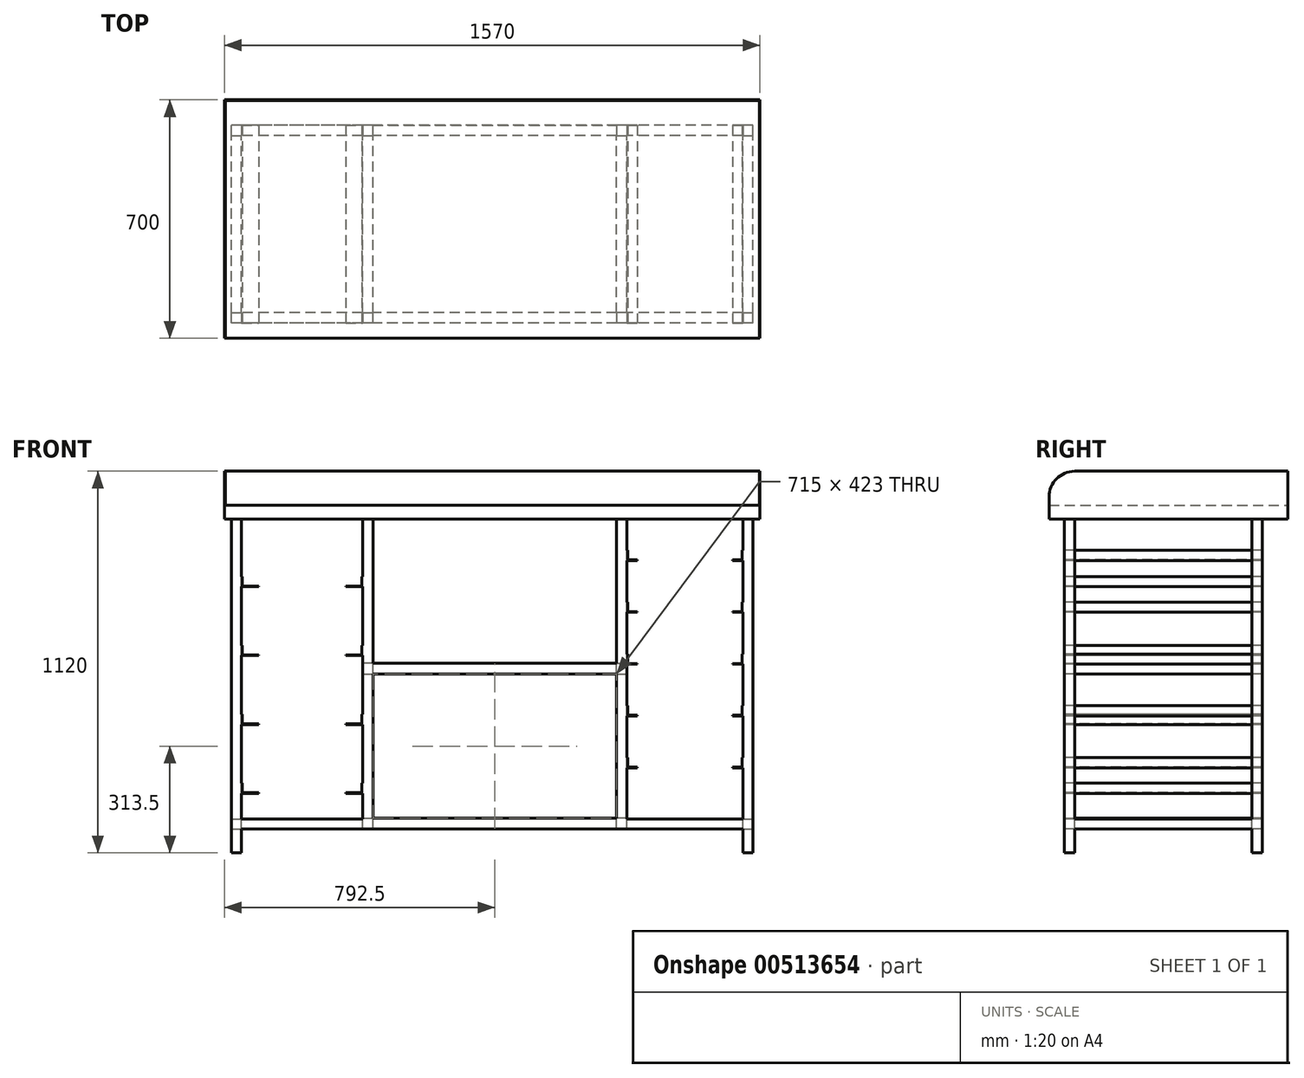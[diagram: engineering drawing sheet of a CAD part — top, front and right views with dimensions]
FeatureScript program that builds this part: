
annotation { "Feature Type Name" : "Feature", "Feature Type Description" : "" }
export const myFeature = defineFeature(function(context is Context, id is Id, definition is map)
    precondition{}
    {
        {
            var Q0;
            Q0=qCreatedBy(makeId("Top.planeOp"),FACE);
            var sketch = newSketch(context, id + "F0", { "sketchPlane" : qUnion([Q0])});
            skLineSegment(sketch, "E0.bottom", {"start": v(785, 350) * mm, "end": v(-785, 350) * mm});
            skLineSegment(sketch, "E0.top", {"start": v(785, -350) * mm, "end": v(-785, -350) * mm});
            skLineSegment(sketch, "E0.left", {"start": v(785, 350) * mm, "end": v(785, -350) * mm});
            skLineSegment(sketch, "E0.right", {"start": v(-785, 350) * mm, "end": v(-785, -350) * mm});
            skPoint(sketch, "E0.middle", {"position": v(0, 0) * mm});
            skSolve(sketch);
        }
        {
            var Q0;
            Q0 = qSketchRegion(id + "F0", true);
            extrude(context, id + "F1", {"entities" : qUnion([Q0]), "depth" : 40 * mm});
        }
        {
            var Q0;
            Q0=makeQuery(id+"F1.opExtrude","CAP_FACE",FACE,{"disambiguationData":[OSD([sQuery(id+"F0.wireOp",EDGE,"E0.bottom"),sQuery(id+"F0.wireOp",EDGE,"E0.top"),sQuery(id+"F0.wireOp",EDGE,"E0.left"),sQuery(id+"F0.wireOp",EDGE,"E0.right")])],"isStart":false});
            var sketch = newSketch(context, id + "F2", { "sketchPlane" : qUnion([Q0])});
            skLineSegment(sketch, "E1", {"start": v(-785, -350) * mm, "end": v(-785, 350) * mm});
            skLineSegment(sketch, "E2", {"start": v(-785, 350) * mm, "end": v(785, 350) * mm});
            skLineSegment(sketch, "E3", {"start": v(785, 350) * mm, "end": v(785, -350) * mm});
            skLineSegment(sketch, "E4", {"start": v(785, -350) * mm, "end": v(783, -350) * mm});
            skLineSegment(sketch, "E5", {"start": v(783, -350) * mm, "end": v(783, 348) * mm});
            skLineSegment(sketch, "E6", {"start": v(783, 348) * mm, "end": v(-783, 348) * mm});
            skLineSegment(sketch, "E7", {"start": v(-783, 348) * mm, "end": v(-783, -350) * mm});
            skLineSegment(sketch, "E8", {"start": v(-783, -350) * mm, "end": v(-785, -350) * mm});
            skSolve(sketch);
        }
        {
            var Q0;
            Q0 = qSketchRegion(id + "F2", true);
            extrude(context, id + "F3", {"entities" : qUnion([Q0]), "operationType" : NewBodyOperationType.ADD, "depth" : 100 * mm});
        }
        {
            var Q0;
            Q0=makeQuery(id+"F3.opExtrude","CAP_EDGE",EDGE,{"disambiguationData":[OSD([sQuery(id+"F2.wireOp",EDGE,"E8")])],"isStart":false});
            var Q1;
            Q1=makeQuery(id+"F3.opExtrude","CAP_EDGE",EDGE,{"disambiguationData":[OSD([sQuery(id+"F2.wireOp",EDGE,"E4")])],"isStart":false});
            fillet(context, id + "F4", {"entities" : qUnion([Q0, Q1]), "radius" : 75 * mm, "tangentPropagation" : true, "allowEdgeOverflow" : false});
        }
        {
            var Q0;
            Q0=makeQuery(id+"F1.opExtrude","CAP_FACE",FACE,{"disambiguationData":[OSD([sQuery(id+"F0.wireOp",EDGE,"E0.bottom"),sQuery(id+"F0.wireOp",EDGE,"E0.top"),sQuery(id+"F0.wireOp",EDGE,"E0.left"),sQuery(id+"F0.wireOp",EDGE,"E0.right")])],"isStart":true});
            var sketch = newSketch(context, id + "F5", { "sketchPlane" : qUnion([Q0])});
            skLineSegment(sketch, "E9.bottom", {"start": v(-735, 305) * mm, "end": v(-765, 305) * mm});
            skLineSegment(sketch, "E9.top", {"start": v(-735, 275) * mm, "end": v(-765, 275) * mm});
            skLineSegment(sketch, "E9.left", {"start": v(-735, 305) * mm, "end": v(-735, 275) * mm});
            skLineSegment(sketch, "E9.right", {"start": v(-765, 305) * mm, "end": v(-765, 275) * mm});
            skPoint(sketch, "E9.middle", {"position": v(-750, 290) * mm});
            skLineSegment(sketch, "E10.bottom", {"start": v(765, 305) * mm, "end": v(735, 305) * mm});
            skLineSegment(sketch, "E10.top", {"start": v(765, 275) * mm, "end": v(735, 275) * mm});
            skLineSegment(sketch, "E10.left", {"start": v(765, 305) * mm, "end": v(765, 275) * mm});
            skLineSegment(sketch, "E10.right", {"start": v(735, 305) * mm, "end": v(735, 275) * mm});
            skPoint(sketch, "E10.middle", {"position": v(750, 290) * mm});
            skPoint(sketch, "E10.middle.positionSnap0", {"position": v(-735, 290) * mm});
            skPoint(sketch, "E10.centerSnap0", {"position": v(-735, 290) * mm});
            skLineSegment(sketch, "E11.bottom", {"start": v(765, -245) * mm, "end": v(735, -245) * mm});
            skLineSegment(sketch, "E11.top", {"start": v(765, -275) * mm, "end": v(735, -275) * mm});
            skLineSegment(sketch, "E11.left", {"start": v(765, -245) * mm, "end": v(765, -275) * mm});
            skLineSegment(sketch, "E11.right", {"start": v(735, -245) * mm, "end": v(735, -275) * mm});
            skPoint(sketch, "E11.middle", {"position": v(750, -260) * mm});
            skLineSegment(sketch, "E12.bottom", {"start": v(-735, -245) * mm, "end": v(-765, -245) * mm});
            skLineSegment(sketch, "E12.top", {"start": v(-735, -275) * mm, "end": v(-765, -275) * mm});
            skLineSegment(sketch, "E12.left", {"start": v(-735, -245) * mm, "end": v(-735, -275) * mm});
            skLineSegment(sketch, "E12.right", {"start": v(-765, -245) * mm, "end": v(-765, -275) * mm});
            skPoint(sketch, "E12.middle", {"position": v(-750, -260) * mm});
            skPoint(sketch, "E12.middle.positionSnap0", {"position": v(735, -260) * mm});
            skPoint(sketch, "E12.centerSnap0", {"position": v(735, -260) * mm});
            skSolve(sketch);
        }
        {
            var Q0;
            Q0 = qSketchRegion(id + "F5", true);
            extrude(context, id + "F6", {"entities" : qUnion([Q0]), "operationType" : NewBodyOperationType.ADD, "depth" : (1050 - 40 - 30) * mm});
        }
        {
            var Q0;
            Q0=qCreatedBy(makeId("Right.planeOp"),FACE);
            var sketch = newSketch(context, id + "F7", { "sketchPlane" : qUnion([Q0])});
            skLineSegment(sketch, "E13.bottom", {"start": v(-275, -880) * mm, "end": v(-305, -880) * mm});
            skLineSegment(sketch, "E13.top", {"start": v(-275, -910) * mm, "end": v(-305, -910) * mm});
            skLineSegment(sketch, "E13.left", {"start": v(-275, -880) * mm, "end": v(-275, -910) * mm});
            skLineSegment(sketch, "E13.right", {"start": v(-305, -880) * mm, "end": v(-305, -910) * mm});
            skPoint(sketch, "E13.middle", {"position": v(-290, -895) * mm});
            skLineSegment(sketch, "E14.bottom", {"start": v(275, -880) * mm, "end": v(245, -880) * mm});
            skLineSegment(sketch, "E14.top", {"start": v(275, -910) * mm, "end": v(245, -910) * mm});
            skLineSegment(sketch, "E14.left", {"start": v(275, -880) * mm, "end": v(275, -910) * mm});
            skLineSegment(sketch, "E14.right", {"start": v(245, -880) * mm, "end": v(245, -910) * mm});
            skPoint(sketch, "E14.middle", {"position": v(260, -895) * mm});
            skSolve(sketch);
        }
        {
            var Q0;
            Q0 = qSketchRegion(id + "F7", true);
            extrude(context, id + "F8", {"entities" : qUnion([Q0]), "operationType" : NewBodyOperationType.ADD, "endBound" : BoundingType.UP_TO_NEXT, "depth" : 25 * mm, "hasSecondDirection" : true, "secondDirectionBound" : SecondDirectionBoundingType.UP_TO_NEXT, "secondDirectionOppositeDirection" : true, "secondDirectionDepth" : 25 * mm});
        }
        {
            var Q0;
            Q0=qCreatedBy(makeId("Front.planeOp"),FACE);
            var sketch = newSketch(context, id + "F9", { "sketchPlane" : qUnion([Q0])});
            skLineSegment(sketch, "E15.bottom", {"start": v(-735, -880) * mm, "end": v(-765, -880) * mm});
            skLineSegment(sketch, "E15.top", {"start": v(-735, -910) * mm, "end": v(-765, -910) * mm});
            skLineSegment(sketch, "E15.left", {"start": v(-735, -880) * mm, "end": v(-735, -910) * mm});
            skLineSegment(sketch, "E15.right", {"start": v(-765, -880) * mm, "end": v(-765, -910) * mm});
            skPoint(sketch, "E15.middle", {"position": v(-750, -895) * mm});
            skLineSegment(sketch, "E16.bottom", {"start": v(765, -880) * mm, "end": v(735, -880) * mm});
            skLineSegment(sketch, "E16.top", {"start": v(765, -910) * mm, "end": v(735, -910) * mm});
            skLineSegment(sketch, "E16.left", {"start": v(765, -880) * mm, "end": v(765, -910) * mm});
            skLineSegment(sketch, "E16.right", {"start": v(735, -880) * mm, "end": v(735, -910) * mm});
            skPoint(sketch, "E16.middle", {"position": v(750, -895) * mm});
            skSolve(sketch);
        }
        {
            var Q0;
            Q0 = qSketchRegion(id + "F9", true);
            extrude(context, id + "F10", {"entities" : qUnion([Q0]), "operationType" : NewBodyOperationType.ADD, "endBound" : BoundingType.UP_TO_NEXT, "depth" : 25 * mm, "hasSecondDirection" : true, "secondDirectionBound" : SecondDirectionBoundingType.UP_TO_NEXT, "secondDirectionOppositeDirection" : true, "secondDirectionDepth" : 25 * mm});
        }
        {
            var Q0;
            Q0=makeQuery(id+"F1.opExtrude","CAP_FACE",FACE,{"disambiguationData":[OSD([sQuery(id+"F0.wireOp",EDGE,"E0.bottom"),sQuery(id+"F0.wireOp",EDGE,"E0.top"),sQuery(id+"F0.wireOp",EDGE,"E0.left"),sQuery(id+"F0.wireOp",EDGE,"E0.right")])],"isStart":true});
            var sketch = newSketch(context, id + "F11", { "sketchPlane" : qUnion([Q0])});
            skLineSegment(sketch, "E17.bottom", {"start": v(-350, 305) * mm, "end": v(-380, 305) * mm});
            skLineSegment(sketch, "E17.top", {"start": v(-350, 275) * mm, "end": v(-380, 275) * mm});
            skLineSegment(sketch, "E17.left", {"start": v(-350, 305) * mm, "end": v(-350, 275) * mm});
            skLineSegment(sketch, "E17.right", {"start": v(-380, 305) * mm, "end": v(-380, 275) * mm});
            skPoint(sketch, "E17.middle", {"position": v(-365, 290) * mm});
            skLineSegment(sketch, "E18.bottom", {"start": v(395, 305) * mm, "end": v(365, 305) * mm});
            skLineSegment(sketch, "E18.top", {"start": v(395, 275) * mm, "end": v(365, 275) * mm});
            skLineSegment(sketch, "E18.left", {"start": v(395, 305) * mm, "end": v(395, 275) * mm});
            skLineSegment(sketch, "E18.right", {"start": v(365, 305) * mm, "end": v(365, 275) * mm});
            skPoint(sketch, "E18.middle", {"position": v(380, 290) * mm});
            skLineSegment(sketch, "E19.bottom", {"start": v(395, -245) * mm, "end": v(365, -245) * mm});
            skLineSegment(sketch, "E19.top", {"start": v(395, -275) * mm, "end": v(365, -275) * mm});
            skLineSegment(sketch, "E19.left", {"start": v(395, -245) * mm, "end": v(395, -275) * mm});
            skLineSegment(sketch, "E19.right", {"start": v(365, -245) * mm, "end": v(365, -275) * mm});
            skPoint(sketch, "E19.middle", {"position": v(380, -260) * mm});
            skPoint(sketch, "E19.middle.positionSnap0", {"position": v(380, 275) * mm});
            skPoint(sketch, "E19.centerSnap0", {"position": v(380, 275) * mm});
            skLineSegment(sketch, "E20.bottom", {"start": v(-350, -245) * mm, "end": v(-380, -245) * mm});
            skLineSegment(sketch, "E20.top", {"start": v(-350, -275) * mm, "end": v(-380, -275) * mm});
            skLineSegment(sketch, "E20.left", {"start": v(-350, -245) * mm, "end": v(-350, -275) * mm});
            skLineSegment(sketch, "E20.right", {"start": v(-380, -245) * mm, "end": v(-380, -275) * mm});
            skPoint(sketch, "E20.middle", {"position": v(-365, -260) * mm});
            skPoint(sketch, "E20.middle.positionSnap0", {"position": v(365, -260) * mm});
            skPoint(sketch, "E20.centerSnap0", {"position": v(365, -260) * mm});
            skSolve(sketch);
        }
        {
            var Q0;
            Q0 = qSketchRegion(id + "F11", true);
            extrude(context, id + "F12", {"entities" : qUnion([Q0]), "operationType" : NewBodyOperationType.ADD, "endBound" : BoundingType.UP_TO_NEXT, "depth" : 25 * mm});
        }
        {
            var Q0;
            Q0=qCreatedBy(makeId("Right.planeOp"),FACE);
            var sketch = newSketch(context, id + "F13", { "sketchPlane" : qUnion([Q0])});
            skLineSegment(sketch, "E21.bottom", {"start": v(-275, -425) * mm, "end": v(-305, -425) * mm});
            skLineSegment(sketch, "E21.top", {"start": v(-275, -455) * mm, "end": v(-305, -455) * mm});
            skLineSegment(sketch, "E21.left", {"start": v(-275, -425) * mm, "end": v(-275, -455) * mm});
            skLineSegment(sketch, "E21.right", {"start": v(-305, -425) * mm, "end": v(-305, -455) * mm});
            skPoint(sketch, "E21.middle", {"position": v(-290, -440) * mm});
            skLineSegment(sketch, "E22.bottom", {"start": v(275, -425) * mm, "end": v(245, -425) * mm});
            skLineSegment(sketch, "E22.top", {"start": v(275, -455) * mm, "end": v(245, -455) * mm});
            skLineSegment(sketch, "E22.left", {"start": v(275, -425) * mm, "end": v(275, -455) * mm});
            skLineSegment(sketch, "E22.right", {"start": v(245, -425) * mm, "end": v(245, -455) * mm});
            skPoint(sketch, "E22.middle", {"position": v(260, -440) * mm});
            skSolve(sketch);
        }
        {
            var Q0;
            Q0 = qSketchRegion(id + "F13", true);
            extrude(context, id + "F14", {"entities" : qUnion([Q0]), "operationType" : NewBodyOperationType.ADD, "endBound" : BoundingType.UP_TO_NEXT, "depth" : 25 * mm, "hasSecondDirection" : true, "secondDirectionBound" : SecondDirectionBoundingType.UP_TO_NEXT, "secondDirectionOppositeDirection" : true, "secondDirectionDepth" : 25 * mm});
        }
        {
            var Q0;
            Q0=qCreatedBy(makeId("Front.planeOp"),FACE);
            var sketch = newSketch(context, id + "F15", { "sketchPlane" : qUnion([Q0])});
            skLineSegment(sketch, "E23.bottom", {"start": v(-350, -425) * mm, "end": v(-380, -425) * mm});
            skLineSegment(sketch, "E23.top", {"start": v(-350, -455) * mm, "end": v(-380, -455) * mm});
            skLineSegment(sketch, "E23.left", {"start": v(-350, -425) * mm, "end": v(-350, -455) * mm});
            skLineSegment(sketch, "E23.right", {"start": v(-380, -425) * mm, "end": v(-380, -455) * mm});
            skPoint(sketch, "E23.middle", {"position": v(-365, -440) * mm});
            skLineSegment(sketch, "E24.bottom", {"start": v(395, -425) * mm, "end": v(365, -425) * mm});
            skLineSegment(sketch, "E24.top", {"start": v(395, -455) * mm, "end": v(365, -455) * mm});
            skLineSegment(sketch, "E24.left", {"start": v(395, -425) * mm, "end": v(395, -455) * mm});
            skLineSegment(sketch, "E24.right", {"start": v(365, -425) * mm, "end": v(365, -455) * mm});
            skPoint(sketch, "E24.middle", {"position": v(380, -440) * mm});
            skLineSegment(sketch, "E25.bottom", {"start": v(395, -880) * mm, "end": v(365, -880) * mm});
            skLineSegment(sketch, "E25.top", {"start": v(395, -910) * mm, "end": v(365, -910) * mm});
            skLineSegment(sketch, "E25.left", {"start": v(395, -880) * mm, "end": v(395, -910) * mm});
            skLineSegment(sketch, "E25.right", {"start": v(365, -880) * mm, "end": v(365, -910) * mm});
            skPoint(sketch, "E25.middle", {"position": v(380, -895) * mm});
            skPoint(sketch, "E25.middle.positionSnap0", {"position": v(380, -455) * mm});
            skPoint(sketch, "E25.centerSnap0", {"position": v(380, -455) * mm});
            skLineSegment(sketch, "E26.bottom", {"start": v(-350, -880) * mm, "end": v(-380, -880) * mm});
            skLineSegment(sketch, "E26.top", {"start": v(-350, -910) * mm, "end": v(-380, -910) * mm});
            skLineSegment(sketch, "E26.left", {"start": v(-350, -880) * mm, "end": v(-350, -910) * mm});
            skLineSegment(sketch, "E26.right", {"start": v(-380, -880) * mm, "end": v(-380, -910) * mm});
            skPoint(sketch, "E26.middle", {"position": v(-365, -895) * mm});
            skSolve(sketch);
        }
        {
            var Q0;
            Q0 = qSketchRegion(id + "F15", true);
            extrude(context, id + "F16", {"entities" : qUnion([Q0]), "operationType" : NewBodyOperationType.ADD, "endBound" : BoundingType.UP_TO_NEXT, "depth" : 25 * mm, "hasSecondDirection" : true, "secondDirectionBound" : SecondDirectionBoundingType.UP_TO_NEXT, "secondDirectionOppositeDirection" : true, "secondDirectionDepth" : 25 * mm});
        }
        {
            var Q0;
            Q0=makeQuery(id+"F14.opExtrude","SWEPT_FACE",FACE,{"disambiguationData":[OSD([sQuery(id+"F13.wireOp",EDGE,"E22.bottom")])]});
            var sketch = newSketch(context, id + "F17", { "sketchPlane" : qUnion([Q0])});
            skLineSegment(sketch, "E27", {"start": v(365, 275) * mm, "end": v(365, 245) * mm});
            skLineSegment(sketch, "E28", {"start": v(365, 245) * mm, "end": v(395, 245) * mm});
            skLineSegment(sketch, "E29", {"start": v(395, 245) * mm, "end": v(395, -275) * mm});
            skLineSegment(sketch, "E30", {"start": v(395, -275) * mm, "end": v(365, -275) * mm});
            skLineSegment(sketch, "E31", {"start": v(365, -275) * mm, "end": v(365, -305) * mm});
            skLineSegment(sketch, "E32", {"start": v(365, -305) * mm, "end": v(-350, -305) * mm});
            skLineSegment(sketch, "E33", {"start": v(-350, -305) * mm, "end": v(-350, -275) * mm});
            skLineSegment(sketch, "E34", {"start": v(-350, -275) * mm, "end": v(-380, -275) * mm});
            skLineSegment(sketch, "E35", {"start": v(-380, -275) * mm, "end": v(-380, 245) * mm});
            skLineSegment(sketch, "E36", {"start": v(-380, 245) * mm, "end": v(-350, 245) * mm});
            skLineSegment(sketch, "E37", {"start": v(-350, 245) * mm, "end": v(-350, 275) * mm});
            skLineSegment(sketch, "E38", {"start": v(-350, 275) * mm, "end": v(365, 275) * mm});
            skSolve(sketch);
        }
        {
            var Q0;
            Q0 = qSketchRegion(id + "F17", true);
            extrude(context, id + "F18", {"entities" : qUnion([Q0]), "operationType" : NewBodyOperationType.ADD, "depth" : 2 * mm});
        }
        {
            var Q0;
            Q0=makeQuery(id+"F16.opExtrude","SWEPT_FACE",FACE,{"disambiguationData":[OSD([sQuery(id+"F15.wireOp",EDGE,"E26.bottom")])]});
            var sketch = newSketch(context, id + "F19", { "sketchPlane" : qUnion([Q0])});
            skLineSegment(sketch, "E39", {"start": v(365, 275) * mm, "end": v(365, 245) * mm});
            skLineSegment(sketch, "E40", {"start": v(365, 245) * mm, "end": v(395, 245) * mm});
            skLineSegment(sketch, "E41", {"start": v(395, 245) * mm, "end": v(395, -275) * mm});
            skLineSegment(sketch, "E42", {"start": v(395, -275) * mm, "end": v(365, -275) * mm});
            skLineSegment(sketch, "E43", {"start": v(365, -275) * mm, "end": v(365, -305) * mm});
            skLineSegment(sketch, "E44", {"start": v(365, -305) * mm, "end": v(-350, -305) * mm});
            skLineSegment(sketch, "E45", {"start": v(-350, -305) * mm, "end": v(-350, -275) * mm});
            skLineSegment(sketch, "E46", {"start": v(-350, -275) * mm, "end": v(-380, -275) * mm});
            skLineSegment(sketch, "E47", {"start": v(-380, -275) * mm, "end": v(-380, 245) * mm});
            skLineSegment(sketch, "E48", {"start": v(-380, 245) * mm, "end": v(-350, 245) * mm});
            skLineSegment(sketch, "E49", {"start": v(-350, 245) * mm, "end": v(-350, 275) * mm});
            skLineSegment(sketch, "E50", {"start": v(-350, 275) * mm, "end": v(365, 275) * mm});
            skSolve(sketch);
        }
        {
            var Q0;
            Q0 = qSketchRegion(id + "F19", true);
            extrude(context, id + "F20", {"entities" : qUnion([Q0]), "operationType" : NewBodyOperationType.ADD, "depth" : 2 * mm});
        }
        {
            var Q0;
            Q0=makeQuery(id+"F20.boolean.opBoolean","MERGE",FACE,{"derivedFrom":[makeQuery(id+"F18.boolean.opBoolean","MERGE",FACE,{"derivedFrom":[makeQuery(id+"F14.boolean.opBoolean","MERGE",FACE,{"derivedFrom":[makeQuery(id+"F12.boolean.opBoolean","MERGE",FACE,{"derivedFrom":[makeQuery(id+"F8.boolean.opBoolean","MERGE",FACE,{"derivedFrom":[makeQuery(id+"F6.opExtrude","SWEPT_FACE",FACE,{"disambiguationData":[OSD([sQuery(id+"F5.wireOp",EDGE,"E9.bottom")])]}),makeQuery(id+"F6.opExtrude","SWEPT_FACE",FACE,{"disambiguationData":[OSD([sQuery(id+"F5.wireOp",EDGE,"E10.bottom")])]}),makeQuery(id+"F8.opExtrude","SWEPT_FACE",FACE,{"disambiguationData":[OSD([sQuery(id+"F7.wireOp",EDGE,"E13.right")])]})]}),makeQuery(id+"F12.opExtrude","SWEPT_FACE",FACE,{"disambiguationData":[OSD([sQuery(id+"F11.wireOp",EDGE,"E17.bottom")])]}),makeQuery(id+"F12.opExtrude","SWEPT_FACE",FACE,{"disambiguationData":[OSD([sQuery(id+"F11.wireOp",EDGE,"E18.bottom")])]})]}),makeQuery(id+"F14.opExtrude","SWEPT_FACE",FACE,{"disambiguationData":[OSD([sQuery(id+"F13.wireOp",EDGE,"E21.right")])]})]}),makeQuery(id+"F18.opExtrude","SWEPT_FACE",FACE,{"disambiguationData":[OSD([sQuery(id+"F17.wireOp",EDGE,"E32")])]})]}),makeQuery(id+"F20.opExtrude","SWEPT_FACE",FACE,{"disambiguationData":[OSD([sQuery(id+"F19.wireOp",EDGE,"E44")])]})]});
            var sketch = newSketch(context, id + "F21", { "sketchPlane" : qUnion([Q0])});
            skLineSegment(sketch, "E51", {"start": v(-735, -775) * mm, "end": v(-735, -805) * mm});
            skLineSegment(sketch, "E52", {"start": v(-735, -805) * mm, "end": v(-685, -805) * mm});
            skLineSegment(sketch, "E53", {"start": v(-685, -805) * mm, "end": v(-685, -803) * mm});
            skLineSegment(sketch, "E54", {"start": v(-685, -803) * mm, "end": v(-733, -803) * mm});
            skLineSegment(sketch, "E55", {"start": v(-733, -803) * mm, "end": v(-733, -775) * mm});
            skLineSegment(sketch, "E56", {"start": v(-733, -775) * mm, "end": v(-735, -775) * mm});
            skLineSegment(sketch, "E57.0.1.0", {"start": v(-735, -603) * mm, "end": v(-685, -603) * mm});
            skLineSegment(sketch, "E57.0.1.1", {"start": v(-685, -601) * mm, "end": v(-733, -601) * mm});
            skLineSegment(sketch, "E57.0.1.2", {"start": v(-733, -601) * mm, "end": v(-733, -573) * mm});
            skLineSegment(sketch, "E57.0.1.3", {"start": v(-735, -573) * mm, "end": v(-735, -603) * mm});
            skLineSegment(sketch, "E57.0.1.4", {"start": v(-685, -603) * mm, "end": v(-685, -601) * mm});
            skLineSegment(sketch, "E57.0.1.5", {"start": v(-733, -573) * mm, "end": v(-735, -573) * mm});
            skLineSegment(sketch, "E57.0.2.0", {"start": v(-735, -401) * mm, "end": v(-685, -401) * mm});
            skLineSegment(sketch, "E57.0.2.1", {"start": v(-685, -399) * mm, "end": v(-733, -399) * mm});
            skLineSegment(sketch, "E57.0.2.2", {"start": v(-733, -399) * mm, "end": v(-733, -371) * mm});
            skLineSegment(sketch, "E57.0.2.3", {"start": v(-735, -371) * mm, "end": v(-735, -401) * mm});
            skLineSegment(sketch, "E57.0.2.4", {"start": v(-685, -401) * mm, "end": v(-685, -399) * mm});
            skLineSegment(sketch, "E57.0.2.5", {"start": v(-733, -371) * mm, "end": v(-735, -371) * mm});
            skLineSegment(sketch, "E57.0.3.0", {"start": v(-735, -199) * mm, "end": v(-685, -199) * mm});
            skLineSegment(sketch, "E57.0.3.1", {"start": v(-685, -197) * mm, "end": v(-733, -197) * mm});
            skLineSegment(sketch, "E57.0.3.2", {"start": v(-733, -197) * mm, "end": v(-733, -169) * mm});
            skLineSegment(sketch, "E57.0.3.3", {"start": v(-735, -169) * mm, "end": v(-735, -199) * mm});
            skLineSegment(sketch, "E57.0.3.4", {"start": v(-685, -199) * mm, "end": v(-685, -197) * mm});
            skLineSegment(sketch, "E57.0.3.5", {"start": v(-733, -169) * mm, "end": v(-735, -169) * mm});
            skLineSegment(sketch, "E57.direction1", {"start": v(-735, -805) * mm, "end": v(-710, -805) * mm, "construction": true});
            skLineSegment(sketch, "E57.direction2", {"start": v(-735, -805) * mm, "end": v(-735, -603) * mm, "construction": true});
            skLineSegment(sketch, "E58", {"start": v(-557.5, -880) * mm, "end": v(-557.5, -90.41) * mm, "construction": true});
            skLineSegment(sketch, "E59.MirrorCS", {"start": v(-430, -805) * mm, "end": v(-430, -803) * mm});
            skLineSegment(sketch, "E60.MirrorCS", {"start": v(-380, -775) * mm, "end": v(-380, -805) * mm});
            skLineSegment(sketch, "E61.MirrorCS", {"start": v(-380, -805) * mm, "end": v(-430, -805) * mm});
            skLineSegment(sketch, "E62.MirrorCS", {"start": v(-380, -805) * mm, "end": v(-405, -805) * mm, "construction": true});
            skLineSegment(sketch, "E63.MirrorCS", {"start": v(-430, -603) * mm, "end": v(-430, -601) * mm});
            skLineSegment(sketch, "E64.MirrorCS", {"start": v(-382, -601) * mm, "end": v(-382, -573) * mm});
            skLineSegment(sketch, "E65.MirrorCS", {"start": v(-382, -803) * mm, "end": v(-382, -775) * mm});
            skLineSegment(sketch, "E66.MirrorCS", {"start": v(-430, -401) * mm, "end": v(-430, -399) * mm});
            skLineSegment(sketch, "E67.MirrorCS", {"start": v(-430, -803) * mm, "end": v(-382, -803) * mm});
            skLineSegment(sketch, "E68.MirrorCS", {"start": v(-380, -573) * mm, "end": v(-380, -603) * mm});
            skLineSegment(sketch, "E69.MirrorCS", {"start": v(-382, -775) * mm, "end": v(-380, -775) * mm});
            skLineSegment(sketch, "E70.MirrorCS", {"start": v(-382, -573) * mm, "end": v(-380, -573) * mm});
            skLineSegment(sketch, "E71.MirrorCS", {"start": v(-382, -371) * mm, "end": v(-380, -371) * mm});
            skLineSegment(sketch, "E72.MirrorCS", {"start": v(-382, -399) * mm, "end": v(-382, -371) * mm});
            skLineSegment(sketch, "E73.MirrorCS", {"start": v(-380, -603) * mm, "end": v(-430, -603) * mm});
            skLineSegment(sketch, "E74.MirrorCS", {"start": v(-430, -399) * mm, "end": v(-382, -399) * mm});
            skLineSegment(sketch, "E75.MirrorCS", {"start": v(-380, -401) * mm, "end": v(-430, -401) * mm});
            skLineSegment(sketch, "E76.MirrorCS", {"start": v(-382, -169) * mm, "end": v(-380, -169) * mm});
            skLineSegment(sketch, "E77.MirrorCS", {"start": v(-380, -371) * mm, "end": v(-380, -401) * mm});
            skLineSegment(sketch, "E78.MirrorCS", {"start": v(-430, -601) * mm, "end": v(-382, -601) * mm});
            skLineSegment(sketch, "E79.MirrorCS", {"start": v(-430, -197) * mm, "end": v(-382, -197) * mm});
            skLineSegment(sketch, "E80.MirrorCS", {"start": v(-382, -197) * mm, "end": v(-382, -169) * mm});
            skLineSegment(sketch, "E81.MirrorCS", {"start": v(-380, -199) * mm, "end": v(-430, -199) * mm});
            skLineSegment(sketch, "E82.MirrorCS", {"start": v(-430, -199) * mm, "end": v(-430, -197) * mm});
            skLineSegment(sketch, "E83.MirrorCS", {"start": v(-380, -169) * mm, "end": v(-380, -199) * mm});
            skLineSegment(sketch, "E84.MirrorCS", {"start": v(-380, -805) * mm, "end": v(-380, -603) * mm, "construction": true});
            skSolve(sketch);
        }
        {
            var Q0;
            Q0 = qSketchRegion(id + "F21", true);
            var Q1;
            Q1=makeQuery(id+"F20.boolean.opBoolean","MERGE",FACE,{"derivedFrom":[makeQuery(id+"F18.boolean.opBoolean","MERGE",FACE,{"derivedFrom":[makeQuery(id+"F14.boolean.opBoolean","MERGE",FACE,{"derivedFrom":[makeQuery(id+"F12.boolean.opBoolean","MERGE",FACE,{"derivedFrom":[makeQuery(id+"F8.boolean.opBoolean","MERGE",FACE,{"derivedFrom":[makeQuery(id+"F6.opExtrude","SWEPT_FACE",FACE,{"disambiguationData":[OSD([sQuery(id+"F5.wireOp",EDGE,"E11.top")])]}),makeQuery(id+"F6.opExtrude","SWEPT_FACE",FACE,{"disambiguationData":[OSD([sQuery(id+"F5.wireOp",EDGE,"E12.top")])]}),makeQuery(id+"F8.opExtrude","SWEPT_FACE",FACE,{"disambiguationData":[OSD([sQuery(id+"F7.wireOp",EDGE,"E14.left")])]})]}),makeQuery(id+"F12.opExtrude","SWEPT_FACE",FACE,{"disambiguationData":[OSD([sQuery(id+"F11.wireOp",EDGE,"E19.top")])]}),makeQuery(id+"F12.opExtrude","SWEPT_FACE",FACE,{"disambiguationData":[OSD([sQuery(id+"F11.wireOp",EDGE,"E20.top")])]})]}),makeQuery(id+"F14.opExtrude","SWEPT_FACE",FACE,{"disambiguationData":[OSD([sQuery(id+"F13.wireOp",EDGE,"E22.left")])]})]}),makeQuery(id+"F18.opExtrude","SWEPT_FACE",FACE,{"disambiguationData":[OSD([sQuery(id+"F17.wireOp",EDGE,"E38")])]})]}),makeQuery(id+"F20.opExtrude","SWEPT_FACE",FACE,{"disambiguationData":[OSD([sQuery(id+"F19.wireOp",EDGE,"E50")])]})]});
            extrude(context, id + "F22", {"entities" : qUnion([Q0]), "operationType" : NewBodyOperationType.ADD, "endBound" : BoundingType.UP_TO_SURFACE, "oppositeDirection" : true, "endBoundEntityFace" : qUnion([Q1]), "depth" : 25 * mm});
        }
        {
            var Q0;
            Q0=makeQuery(id+"F22.boolean.opBoolean","MERGE",FACE,{"derivedFrom":[makeQuery(id+"F20.boolean.opBoolean","MERGE",FACE,{"derivedFrom":[makeQuery(id+"F18.boolean.opBoolean","MERGE",FACE,{"derivedFrom":[makeQuery(id+"F14.boolean.opBoolean","MERGE",FACE,{"derivedFrom":[makeQuery(id+"F12.boolean.opBoolean","MERGE",FACE,{"derivedFrom":[makeQuery(id+"F8.boolean.opBoolean","MERGE",FACE,{"derivedFrom":[makeQuery(id+"F6.opExtrude","SWEPT_FACE",FACE,{"disambiguationData":[OSD([sQuery(id+"F5.wireOp",EDGE,"E9.bottom")])]}),makeQuery(id+"F6.opExtrude","SWEPT_FACE",FACE,{"disambiguationData":[OSD([sQuery(id+"F5.wireOp",EDGE,"E10.bottom")])]}),makeQuery(id+"F8.opExtrude","SWEPT_FACE",FACE,{"disambiguationData":[OSD([sQuery(id+"F7.wireOp",EDGE,"E13.right")])]})]}),makeQuery(id+"F12.opExtrude","SWEPT_FACE",FACE,{"disambiguationData":[OSD([sQuery(id+"F11.wireOp",EDGE,"E17.bottom")])]}),makeQuery(id+"F12.opExtrude","SWEPT_FACE",FACE,{"disambiguationData":[OSD([sQuery(id+"F11.wireOp",EDGE,"E18.bottom")])]})]}),makeQuery(id+"F14.opExtrude","SWEPT_FACE",FACE,{"disambiguationData":[OSD([sQuery(id+"F13.wireOp",EDGE,"E21.right")])]})]}),makeQuery(id+"F18.opExtrude","SWEPT_FACE",FACE,{"disambiguationData":[OSD([sQuery(id+"F17.wireOp",EDGE,"E32")])]})]}),makeQuery(id+"F20.opExtrude","SWEPT_FACE",FACE,{"disambiguationData":[OSD([sQuery(id+"F19.wireOp",EDGE,"E44")])]})]}),makeQuery(id+"F22.opExtrude","CAP_FACE",FACE,{"disambiguationData":[OSD([sQuery(id+"F21.wireOp",EDGE,"E51"),sQuery(id+"F21.wireOp",EDGE,"E52"),sQuery(id+"F21.wireOp",EDGE,"E53"),sQuery(id+"F21.wireOp",EDGE,"E54"),sQuery(id+"F21.wireOp",EDGE,"E55"),sQuery(id+"F21.wireOp",EDGE,"E56")])],"isStart":true}),makeQuery(id+"F22.opExtrude","CAP_FACE",FACE,{"disambiguationData":[OSD([sQuery(id+"F21.wireOp",EDGE,"E57.0.1.0"),sQuery(id+"F21.wireOp",EDGE,"E57.0.1.1"),sQuery(id+"F21.wireOp",EDGE,"E57.0.1.2"),sQuery(id+"F21.wireOp",EDGE,"E57.0.1.3"),sQuery(id+"F21.wireOp",EDGE,"E57.0.1.4"),sQuery(id+"F21.wireOp",EDGE,"E57.0.1.5")])],"isStart":true}),makeQuery(id+"F22.opExtrude","CAP_FACE",FACE,{"disambiguationData":[OSD([sQuery(id+"F21.wireOp",EDGE,"E57.0.2.0"),sQuery(id+"F21.wireOp",EDGE,"E57.0.2.1"),sQuery(id+"F21.wireOp",EDGE,"E57.0.2.2"),sQuery(id+"F21.wireOp",EDGE,"E57.0.2.3"),sQuery(id+"F21.wireOp",EDGE,"E57.0.2.4"),sQuery(id+"F21.wireOp",EDGE,"E57.0.2.5")])],"isStart":true}),makeQuery(id+"F22.opExtrude","CAP_FACE",FACE,{"disambiguationData":[OSD([sQuery(id+"F21.wireOp",EDGE,"E57.0.3.0"),sQuery(id+"F21.wireOp",EDGE,"E57.0.3.1"),sQuery(id+"F21.wireOp",EDGE,"E57.0.3.2"),sQuery(id+"F21.wireOp",EDGE,"E57.0.3.3"),sQuery(id+"F21.wireOp",EDGE,"E57.0.3.4"),sQuery(id+"F21.wireOp",EDGE,"E57.0.3.5")])],"isStart":true}),makeQuery(id+"F22.opExtrude","CAP_FACE",FACE,{"disambiguationData":[OSD([sQuery(id+"F21.wireOp",EDGE,"E59.MirrorCS"),sQuery(id+"F21.wireOp",EDGE,"E60.MirrorCS"),sQuery(id+"F21.wireOp",EDGE,"E61.MirrorCS"),sQuery(id+"F21.wireOp",EDGE,"E65.MirrorCS"),sQuery(id+"F21.wireOp",EDGE,"E67.MirrorCS"),sQuery(id+"F21.wireOp",EDGE,"E69.MirrorCS")])],"isStart":true}),makeQuery(id+"F22.opExtrude","CAP_FACE",FACE,{"disambiguationData":[OSD([sQuery(id+"F21.wireOp",EDGE,"E63.MirrorCS"),sQuery(id+"F21.wireOp",EDGE,"E64.MirrorCS"),sQuery(id+"F21.wireOp",EDGE,"E68.MirrorCS"),sQuery(id+"F21.wireOp",EDGE,"E70.MirrorCS"),sQuery(id+"F21.wireOp",EDGE,"E73.MirrorCS"),sQuery(id+"F21.wireOp",EDGE,"E78.MirrorCS")])],"isStart":true}),makeQuery(id+"F22.opExtrude","CAP_FACE",FACE,{"disambiguationData":[OSD([sQuery(id+"F21.wireOp",EDGE,"E66.MirrorCS"),sQuery(id+"F21.wireOp",EDGE,"E71.MirrorCS"),sQuery(id+"F21.wireOp",EDGE,"E72.MirrorCS"),sQuery(id+"F21.wireOp",EDGE,"E74.MirrorCS"),sQuery(id+"F21.wireOp",EDGE,"E75.MirrorCS"),sQuery(id+"F21.wireOp",EDGE,"E77.MirrorCS")])],"isStart":true}),makeQuery(id+"F22.opExtrude","CAP_FACE",FACE,{"disambiguationData":[OSD([sQuery(id+"F21.wireOp",EDGE,"E76.MirrorCS"),sQuery(id+"F21.wireOp",EDGE,"E79.MirrorCS"),sQuery(id+"F21.wireOp",EDGE,"E80.MirrorCS"),sQuery(id+"F21.wireOp",EDGE,"E81.MirrorCS"),sQuery(id+"F21.wireOp",EDGE,"E82.MirrorCS"),sQuery(id+"F21.wireOp",EDGE,"E83.MirrorCS")])],"isStart":true})]});
            var sketch = newSketch(context, id + "F23", { "sketchPlane" : qUnion([Q0])});
            skLineSegment(sketch, "E85", {"start": v(395, -700) * mm, "end": v(395, -730) * mm});
            skLineSegment(sketch, "E86", {"start": v(395, -730) * mm, "end": v(425, -730) * mm});
            skLineSegment(sketch, "E87", {"start": v(425, -730) * mm, "end": v(425, -728) * mm});
            skLineSegment(sketch, "E88", {"start": v(425, -728) * mm, "end": v(397, -728) * mm});
            skLineSegment(sketch, "E89", {"start": v(397, -728) * mm, "end": v(397, -700) * mm});
            skLineSegment(sketch, "E90", {"start": v(397, -700) * mm, "end": v(395, -700) * mm});
            skLineSegment(sketch, "E91.0.1.0", {"start": v(395, -548) * mm, "end": v(395, -578) * mm});
            skLineSegment(sketch, "E91.0.1.1", {"start": v(395, -578) * mm, "end": v(425, -578) * mm});
            skLineSegment(sketch, "E91.0.1.2", {"start": v(425, -576) * mm, "end": v(397, -576) * mm});
            skLineSegment(sketch, "E91.0.1.3", {"start": v(397, -576) * mm, "end": v(397, -548) * mm});
            skLineSegment(sketch, "E91.0.1.4", {"start": v(425, -578) * mm, "end": v(425, -576) * mm});
            skLineSegment(sketch, "E91.0.1.5", {"start": v(397, -548) * mm, "end": v(395, -548) * mm});
            skLineSegment(sketch, "E91.0.2.0", {"start": v(395, -396) * mm, "end": v(395, -426) * mm});
            skLineSegment(sketch, "E91.0.2.1", {"start": v(395, -426) * mm, "end": v(425, -426) * mm});
            skLineSegment(sketch, "E91.0.2.2", {"start": v(425, -424) * mm, "end": v(397, -424) * mm});
            skLineSegment(sketch, "E91.0.2.3", {"start": v(397, -424) * mm, "end": v(397, -396) * mm});
            skLineSegment(sketch, "E91.0.2.4", {"start": v(425, -426) * mm, "end": v(425, -424) * mm});
            skLineSegment(sketch, "E91.0.2.5", {"start": v(397, -396) * mm, "end": v(395, -396) * mm});
            skLineSegment(sketch, "E91.0.3.0", {"start": v(395, -244) * mm, "end": v(395, -274) * mm});
            skLineSegment(sketch, "E91.0.3.1", {"start": v(395, -274) * mm, "end": v(425, -274) * mm});
            skLineSegment(sketch, "E91.0.3.2", {"start": v(425, -272) * mm, "end": v(397, -272) * mm});
            skLineSegment(sketch, "E91.0.3.3", {"start": v(397, -272) * mm, "end": v(397, -244) * mm});
            skLineSegment(sketch, "E91.0.3.4", {"start": v(425, -274) * mm, "end": v(425, -272) * mm});
            skLineSegment(sketch, "E91.0.3.5", {"start": v(397, -244) * mm, "end": v(395, -244) * mm});
            skLineSegment(sketch, "E91.0.4.0", {"start": v(395, -92) * mm, "end": v(395, -122) * mm});
            skLineSegment(sketch, "E91.0.4.1", {"start": v(395, -122) * mm, "end": v(425, -122) * mm});
            skLineSegment(sketch, "E91.0.4.2", {"start": v(425, -120) * mm, "end": v(397, -120) * mm});
            skLineSegment(sketch, "E91.0.4.3", {"start": v(397, -120) * mm, "end": v(397, -92) * mm});
            skLineSegment(sketch, "E91.0.4.4", {"start": v(425, -122) * mm, "end": v(425, -120) * mm});
            skLineSegment(sketch, "E91.0.4.5", {"start": v(397, -92) * mm, "end": v(395, -92) * mm});
            skLineSegment(sketch, "E91.direction1", {"start": v(395, -730) * mm, "end": v(420, -730) * mm, "construction": true});
            skLineSegment(sketch, "E91.direction2", {"start": v(395, -730) * mm, "end": v(395, -578) * mm, "construction": true});
            skLineSegment(sketch, "E92", {"start": v(565, -880) * mm, "end": v(565, -74.88) * mm, "construction": true});
            skLineSegment(sketch, "E93.MirrorCS", {"start": v(733, -244) * mm, "end": v(735, -244) * mm});
            skLineSegment(sketch, "E94.MirrorCS", {"start": v(733, -92) * mm, "end": v(735, -92) * mm});
            skLineSegment(sketch, "E95.MirrorCS", {"start": v(705, -426) * mm, "end": v(705, -424) * mm});
            skLineSegment(sketch, "E96.MirrorCS", {"start": v(733, -396) * mm, "end": v(735, -396) * mm});
            skLineSegment(sketch, "E97.MirrorCS", {"start": v(735, -730) * mm, "end": v(705, -730) * mm});
            skLineSegment(sketch, "E98.MirrorCS", {"start": v(735, -548) * mm, "end": v(735, -578) * mm});
            skLineSegment(sketch, "E99.MirrorCS", {"start": v(735, -578) * mm, "end": v(705, -578) * mm});
            skLineSegment(sketch, "E100.MirrorCS", {"start": v(733, -120) * mm, "end": v(733, -92) * mm});
            skLineSegment(sketch, "E101.MirrorCS", {"start": v(733, -272) * mm, "end": v(733, -244) * mm});
            skLineSegment(sketch, "E102.MirrorCS", {"start": v(735, -730) * mm, "end": v(710, -730) * mm, "construction": true});
            skLineSegment(sketch, "E103.MirrorCS", {"start": v(705, -122) * mm, "end": v(705, -120) * mm});
            skLineSegment(sketch, "E104.MirrorCS", {"start": v(735, -426) * mm, "end": v(705, -426) * mm});
            skLineSegment(sketch, "E105.MirrorCS", {"start": v(733, -424) * mm, "end": v(733, -396) * mm});
            skLineSegment(sketch, "E106.MirrorCS", {"start": v(735, -700) * mm, "end": v(735, -730) * mm});
            skLineSegment(sketch, "E107.MirrorCS", {"start": v(705, -274) * mm, "end": v(705, -272) * mm});
            skLineSegment(sketch, "E108.MirrorCS", {"start": v(705, -730) * mm, "end": v(705, -728) * mm});
            skLineSegment(sketch, "E109.MirrorCS", {"start": v(705, -576) * mm, "end": v(733, -576) * mm});
            skLineSegment(sketch, "E110.MirrorCS", {"start": v(733, -576) * mm, "end": v(733, -548) * mm});
            skLineSegment(sketch, "E111.MirrorCS", {"start": v(735, -92) * mm, "end": v(735, -122) * mm});
            skLineSegment(sketch, "E112.MirrorCS", {"start": v(705, -424) * mm, "end": v(733, -424) * mm});
            skLineSegment(sketch, "E113.MirrorCS", {"start": v(705, -728) * mm, "end": v(733, -728) * mm});
            skLineSegment(sketch, "E114.MirrorCS", {"start": v(733, -728) * mm, "end": v(733, -700) * mm});
            skLineSegment(sketch, "E115.MirrorCS", {"start": v(733, -700) * mm, "end": v(735, -700) * mm});
            skLineSegment(sketch, "E116.MirrorCS", {"start": v(705, -578) * mm, "end": v(705, -576) * mm});
            skLineSegment(sketch, "E117.MirrorCS", {"start": v(733, -548) * mm, "end": v(735, -548) * mm});
            skLineSegment(sketch, "E118.MirrorCS", {"start": v(735, -122) * mm, "end": v(705, -122) * mm});
            skLineSegment(sketch, "E119.MirrorCS", {"start": v(735, -396) * mm, "end": v(735, -426) * mm});
            skLineSegment(sketch, "E120.MirrorCS", {"start": v(735, -244) * mm, "end": v(735, -274) * mm});
            skLineSegment(sketch, "E121.MirrorCS", {"start": v(705, -120) * mm, "end": v(733, -120) * mm});
            skLineSegment(sketch, "E122.MirrorCS", {"start": v(735, -274) * mm, "end": v(705, -274) * mm});
            skLineSegment(sketch, "E123.MirrorCS", {"start": v(705, -272) * mm, "end": v(733, -272) * mm});
            skLineSegment(sketch, "E124.MirrorCS", {"start": v(735, -730) * mm, "end": v(735, -578) * mm, "construction": true});
            skSolve(sketch);
        }
        {
            var Q0;
            Q0 = qSketchRegion(id + "F23", true);
            var Q1;
            {var subQ0=sQuery(id+"F19.wireOp",EDGE,"E50");var subQ1=sQuery(id+"F17.wireOp",EDGE,"E38");var subQ2=sQuery(id+"F13.wireOp",EDGE,"E22.left");var subQ3=sQuery(id+"F11.wireOp",EDGE,"E20.top");var subQ4=sQuery(id+"F11.wireOp",EDGE,"E19.top");var subQ5=sQuery(id+"F7.wireOp",EDGE,"E14.left");var subQ6=sQuery(id+"F5.wireOp",EDGE,"E12.top");var subQ7=sQuery(id+"F5.wireOp",EDGE,"E11.top");Q1=makeQuery(id+"F22.boolean.opBoolean","MERGE",FACE,{"derivedFrom":[makeQuery(id+"F20.boolean.opBoolean","MERGE",FACE,{"derivedFrom":[makeQuery(id+"F18.boolean.opBoolean","MERGE",FACE,{"derivedFrom":[makeQuery(id+"F14.boolean.opBoolean","MERGE",FACE,{"derivedFrom":[makeQuery(id+"F12.boolean.opBoolean","MERGE",FACE,{"derivedFrom":[makeQuery(id+"F8.boolean.opBoolean","MERGE",FACE,{"derivedFrom":[makeQuery(id+"F6.opExtrude","SWEPT_FACE",FACE,{"disambiguationData":[OSD([subQ7])]}),makeQuery(id+"F6.opExtrude","SWEPT_FACE",FACE,{"disambiguationData":[OSD([subQ6])]}),makeQuery(id+"F8.opExtrude","SWEPT_FACE",FACE,{"disambiguationData":[OSD([subQ5])]})]}),makeQuery(id+"F12.opExtrude","SWEPT_FACE",FACE,{"disambiguationData":[OSD([subQ4])]}),makeQuery(id+"F12.opExtrude","SWEPT_FACE",FACE,{"disambiguationData":[OSD([subQ3])]})]}),makeQuery(id+"F14.opExtrude","SWEPT_FACE",FACE,{"disambiguationData":[OSD([subQ2])]})]}),makeQuery(id+"F18.opExtrude","SWEPT_FACE",FACE,{"disambiguationData":[OSD([subQ1])]})]}),makeQuery(id+"F20.opExtrude","SWEPT_FACE",FACE,{"disambiguationData":[OSD([subQ0])]})]}),makeQuery(id+"F22.opExtrude","CAP_FACE",FACE,{"disambiguationData":[OSD([subQ7,subQ6,subQ5,subQ4,subQ3,subQ2,subQ1,subQ0]),ownerDisambiguation([makeQuery(id+"F21.imprint","IMPRINT",EDGE,{"derivedFrom":sQuery(id+"F21.wireOp",EDGE,"E51")})])],"isStart":false}),makeQuery(id+"F22.opExtrude","CAP_FACE",FACE,{"disambiguationData":[OSD([subQ7,subQ6,subQ5,subQ4,subQ3,subQ2,subQ1,subQ0]),ownerDisambiguation([makeQuery(id+"F21.imprint","IMPRINT",EDGE,{"derivedFrom":sQuery(id+"F21.wireOp",EDGE,"E57.0.1.0")})])],"isStart":false}),makeQuery(id+"F22.opExtrude","CAP_FACE",FACE,{"disambiguationData":[OSD([subQ7,subQ6,subQ5,subQ4,subQ3,subQ2,subQ1,subQ0]),ownerDisambiguation([makeQuery(id+"F21.imprint","IMPRINT",EDGE,{"derivedFrom":sQuery(id+"F21.wireOp",EDGE,"E57.0.2.0")})])],"isStart":false}),makeQuery(id+"F22.opExtrude","CAP_FACE",FACE,{"disambiguationData":[OSD([subQ7,subQ6,subQ5,subQ4,subQ3,subQ2,subQ1,subQ0]),ownerDisambiguation([makeQuery(id+"F21.imprint","IMPRINT",EDGE,{"derivedFrom":sQuery(id+"F21.wireOp",EDGE,"E57.0.3.0")})])],"isStart":false}),makeQuery(id+"F22.opExtrude","CAP_FACE",FACE,{"disambiguationData":[OSD([subQ7,subQ6,subQ5,subQ4,subQ3,subQ2,subQ1,subQ0]),ownerDisambiguation([makeQuery(id+"F21.imprint","IMPRINT",EDGE,{"derivedFrom":sQuery(id+"F21.wireOp",EDGE,"E59.MirrorCS")})])],"isStart":false}),makeQuery(id+"F22.opExtrude","CAP_FACE",FACE,{"disambiguationData":[OSD([subQ7,subQ6,subQ5,subQ4,subQ3,subQ2,subQ1,subQ0]),ownerDisambiguation([makeQuery(id+"F21.imprint","IMPRINT",EDGE,{"derivedFrom":sQuery(id+"F21.wireOp",EDGE,"E63.MirrorCS")})])],"isStart":false}),makeQuery(id+"F22.opExtrude","CAP_FACE",FACE,{"disambiguationData":[OSD([subQ7,subQ6,subQ5,subQ4,subQ3,subQ2,subQ1,subQ0]),ownerDisambiguation([makeQuery(id+"F21.imprint","IMPRINT",EDGE,{"derivedFrom":sQuery(id+"F21.wireOp",EDGE,"E66.MirrorCS")})])],"isStart":false}),makeQuery(id+"F22.opExtrude","CAP_FACE",FACE,{"disambiguationData":[OSD([subQ7,subQ6,subQ5,subQ4,subQ3,subQ2,subQ1,subQ0]),ownerDisambiguation([makeQuery(id+"F21.imprint","IMPRINT",EDGE,{"derivedFrom":sQuery(id+"F21.wireOp",EDGE,"E76.MirrorCS")})])],"isStart":false})]});}
            extrude(context, id + "F24", {"entities" : qUnion([Q0]), "operationType" : NewBodyOperationType.ADD, "endBound" : BoundingType.UP_TO_SURFACE, "oppositeDirection" : true, "endBoundEntityFace" : qUnion([Q1]), "depth" : 25 * mm});
        }
    });
